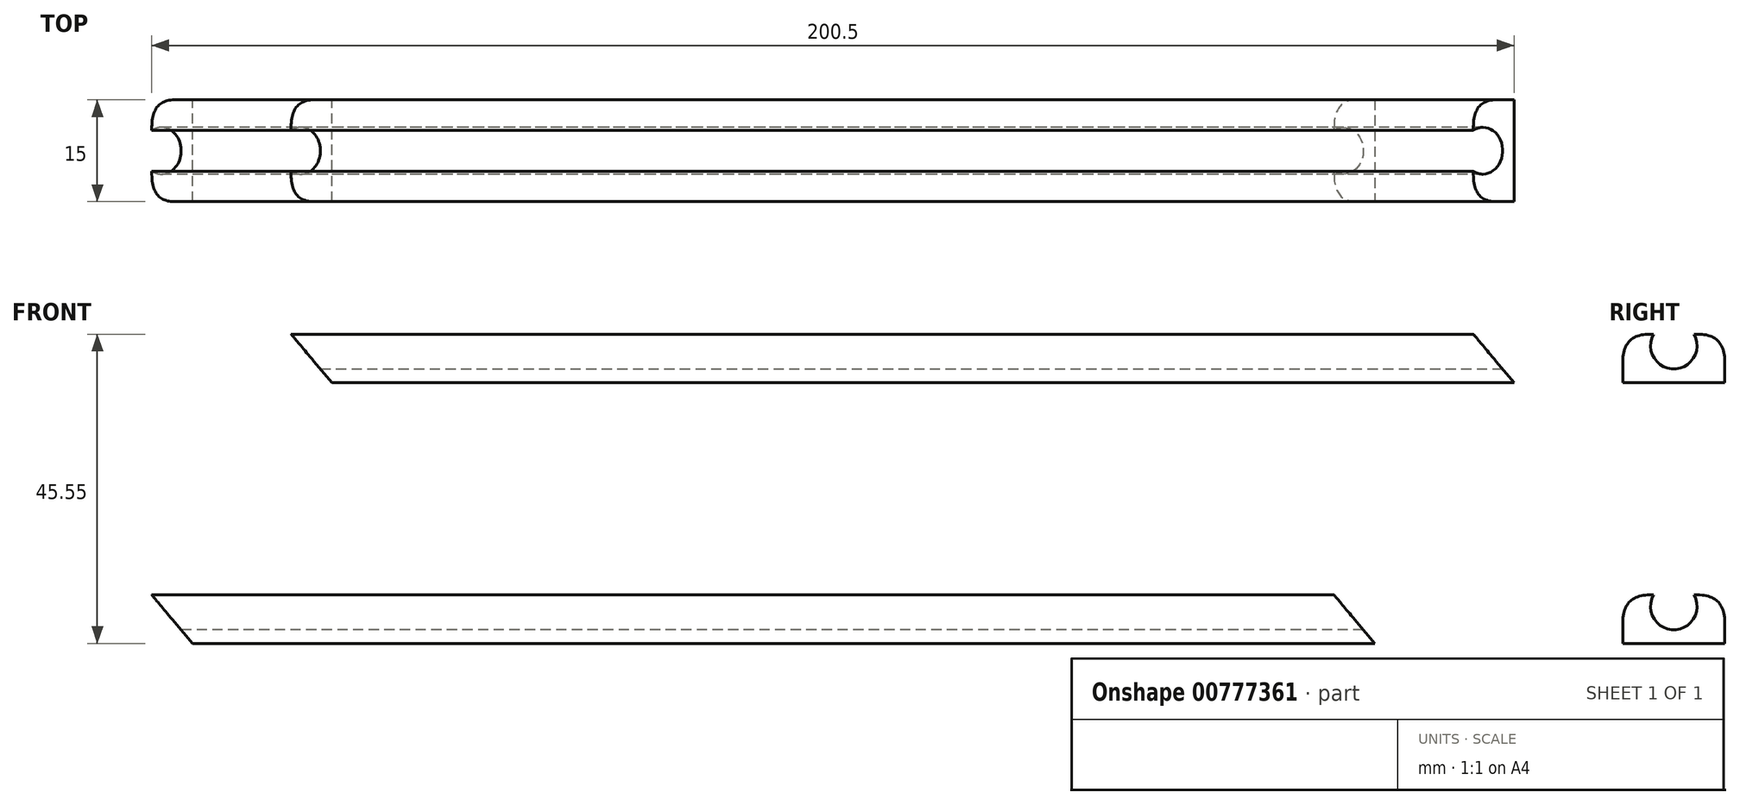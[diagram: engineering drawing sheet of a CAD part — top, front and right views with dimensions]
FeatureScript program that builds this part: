
annotation { "Feature Type Name" : "Feature", "Feature Type Description" : "" }
export const myFeature = defineFeature(function(context is Context, id is Id, definition is map)
    precondition{}
    {
        {
            var Q0;
            Q0=qCreatedBy(makeId("Top.planeOp"),FACE);
            var sketch = newSketch(context, id + "F0", { "sketchPlane" : qUnion([Q0])});
            skLineSegment(sketch, "E0.bottom", {"start": v(90, 7.5) * mm, "end": v(-90, 7.5) * mm});
            skLineSegment(sketch, "E0.top", {"start": v(90, -7.5) * mm, "end": v(-90, -7.5) * mm});
            skLineSegment(sketch, "E0.left", {"start": v(90, 7.5) * mm, "end": v(90, -7.5) * mm});
            skLineSegment(sketch, "E0.right", {"start": v(-90, 7.5) * mm, "end": v(-90, -7.5) * mm});
            skPoint(sketch, "E0.middle", {"position": v(0, 0) * mm});
            skSolve(sketch);
        }
        {
            var Q0;
            Q0 = qSketchRegion(id + "F0", true);
            extrude(context, id + "F1", {"entities" : qUnion([Q0]), "depth" : 7.15 * mm, "offsetDistance" : 25.4 * mm});
        }
        {
            var Q0;
            Q0=makeQuery(id+"F1.opExtrude","SWEPT_FACE",FACE,{"disambiguationData":[OSD([sQuery(id+"F0.wireOp",EDGE,"E0.right")])]});
            var sketch = newSketch(context, id + "F2", { "sketchPlane" : qUnion([Q0])});
            skCircle(sketch, "E1", {"center": v(0, 5.45) * mm, "radius": 3.45 * mm});
            skSolve(sketch);
        }
        {
            var Q0;
            {var subQ0=sQuery(id+"F2.wireOp",EDGE,"E1");var subQ1=makeQuery(id+"F1.opExtrude","CAP_EDGE",EDGE,{"disambiguationData":[OSD([sQuery(id+"F0.wireOp",EDGE,"E0.right")])],"isStart":false});var subQ2=makeQuery(id+"F2.imprint","INTERSECT",VERTEX,{"disambiguationData":[OD(0.0)],"derivedFrom":[subQ1,subQ0]});Q0=makeQuery(id+"F2.imprint","IMPRINT",FACE,{"disambiguationData":[TD([[makeQuery(id+"F2.imprint","IMPRINT",EDGE,{"disambiguationData":[TD([[subQ2,-1.0]])],"derivedFrom":subQ0}),1.0]])]});}
            extrude(context, id + "F3", {"entities" : qUnion([Q0]), "operationType" : NewBodyOperationType.REMOVE, "oppositeDirection" : true, "depth" : 180 * mm, "offsetDistance" : 25 * mm});
        }
        {
            var Q0;
            Q0=makeQuery(id+"F1.opExtrude","CAP_EDGE",EDGE,{"disambiguationData":[OSD([sQuery(id+"F0.wireOp",EDGE,"E0.right")])],"isStart":true});
            chamfer(context, id + "F4", {"entities" : qUnion([Q0]), "chamferType" : ChamferType.OFFSET_ANGLE, "width" : 7.15 * mm, "oppositeDirection" : false, "angle" : 40 * degree, "tangentPropagation" : true});
        }
        {
            var Q0;
            {var subQ0=sQuery(id+"F0.wireOp",EDGE,"E0.left");var subQ1=sQuery(id+"F0.wireOp",EDGE,"E0.top");Q0=makeQuery(id+"F3.boolean.opBoolean","SPLIT",EDGE,{"disambiguationData":[TD([makeQuery(id+"F1.opExtrude","SWEPT_FACE",FACE,{"disambiguationData":[OSD([subQ1])]})])],"derivedFrom":makeQuery(id+"F1.opExtrude","CAP_EDGE",EDGE,{"disambiguationData":[OSD([subQ0])],"isStart":false})});}
            var Q1;
            {var subQ0=sQuery(id+"F0.wireOp",EDGE,"E0.bottom");var subQ1=sQuery(id+"F0.wireOp",EDGE,"E0.left");Q1=makeQuery(id+"F3.boolean.opBoolean","SPLIT",EDGE,{"disambiguationData":[TD([makeQuery(id+"F1.opExtrude","SWEPT_FACE",FACE,{"disambiguationData":[OSD([subQ0])]})])],"derivedFrom":makeQuery(id+"F1.opExtrude","CAP_EDGE",EDGE,{"disambiguationData":[OSD([subQ1])],"isStart":false})});}
            chamfer(context, id + "F5", {"entities" : qUnion([Q0, Q1]), "chamferType" : ChamferType.OFFSET_ANGLE, "width" : 7.15 * mm, "oppositeDirection" : false, "angle" : 40 * degree, "tangentPropagation" : true});
        }
        {
            var Q0;
            Q0=makeQuery(id+"F1.opExtrude","CAP_EDGE",EDGE,{"disambiguationData":[OSD([sQuery(id+"F0.wireOp",EDGE,"E0.top")])],"isStart":false});
            var Q1;
            Q1=makeQuery(id+"F1.opExtrude","CAP_EDGE",EDGE,{"disambiguationData":[OSD([sQuery(id+"F0.wireOp",EDGE,"E0.bottom")])],"isStart":false});
            fillet(context, id + "F6", {"entities" : qUnion([Q0, Q1]), "radius" : 4 * mm, "tangentPropagation" : true, "rho" : 0.5, "crossSection" : FilletCrossSection.CONIC, "allowEdgeOverflow" : false});
        }
        {
            var Q0;
            Q0=makeQuery(id+"F1.opExtrude","SWEPT_BODY",BODY,{"disambiguationData":[OSD([sQuery(id+"F0.wireOp",EDGE,"E0.bottom"),sQuery(id+"F0.wireOp",EDGE,"E0.top"),sQuery(id+"F0.wireOp",EDGE,"E0.left"),sQuery(id+"F0.wireOp",EDGE,"E0.right")])]});
            transform(context, id + "F7", {"entities" : qUnion([Q0]), "transformType" : TransformType.TRANSLATION_3D, "dx" : 0 * mm, "dy" : 37.9 * mm, "dz" : 0 * mm, "makeCopy" : true});
        }
        {
            var Q0;
            Q0=makeQuery(id+"F7.opPattern","COPY",BODY,{"derivedFrom":makeQuery(id+"F1.opExtrude","SWEPT_BODY",BODY,{"disambiguationData":[OSD([sQuery(id+"F0.wireOp",EDGE,"E0.bottom"),sQuery(id+"F0.wireOp",EDGE,"E0.top"),sQuery(id+"F0.wireOp",EDGE,"E0.left"),sQuery(id+"F0.wireOp",EDGE,"E0.right")])]}),"instanceName":"1"});
            deleteBodies(context, id + "F8", {"entities" : qUnion([Q0])});
        }
        {
            var Q0;
            Q0=makeQuery(id+"F1.opExtrude","SWEPT_BODY",BODY,{"disambiguationData":[OSD([sQuery(id+"F0.wireOp",EDGE,"E0.bottom"),sQuery(id+"F0.wireOp",EDGE,"E0.top"),sQuery(id+"F0.wireOp",EDGE,"E0.left"),sQuery(id+"F0.wireOp",EDGE,"E0.right")])]});
            transform(context, id + "F9", {"entities" : qUnion([Q0]), "transformType" : TransformType.TRANSLATION_3D, "dx" : 20.5 * mm, "dy" : 0 * mm, "dz" : 38.4 * mm, "makeCopy" : true});
        }
    });
